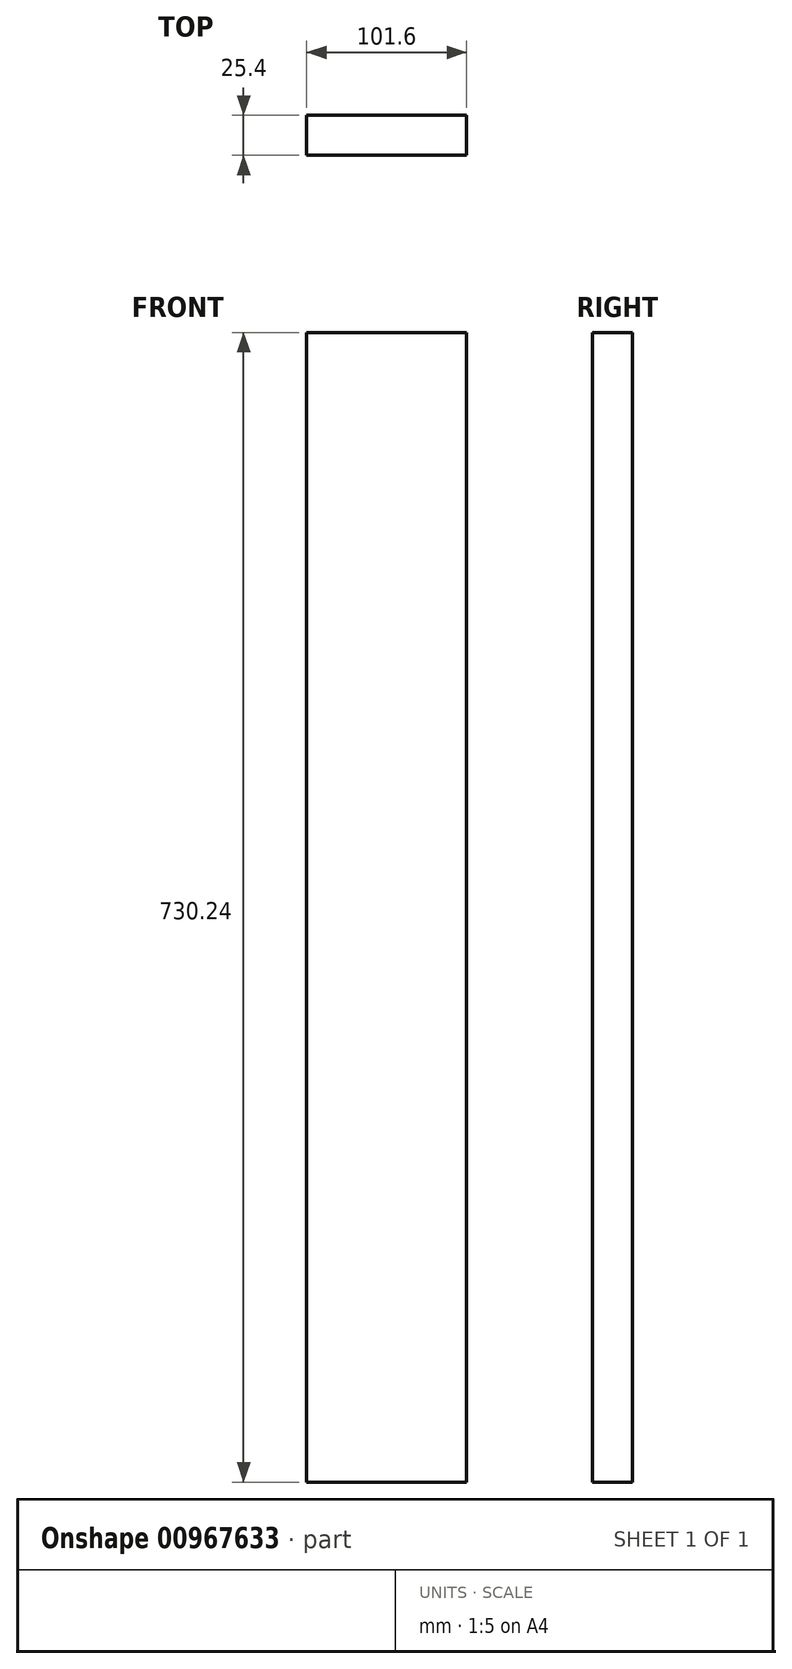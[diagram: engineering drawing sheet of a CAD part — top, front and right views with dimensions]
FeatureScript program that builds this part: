
annotation { "Feature Type Name" : "Feature", "Feature Type Description" : "" }
export const myFeature = defineFeature(function(context is Context, id is Id, definition is map)
    precondition{}
    {
        {
            var Q0;
            Q0=qCreatedBy(makeId("Front.planeOp"),FACE);
            var sketch = newSketch(context, id + "F0", { "sketchPlane" : qUnion([Q0])});
            skLineSegment(sketch, "E0.bottom", {"start": v(50.8, 365.12) * mm, "end": v(-50.8, 365.12) * mm});
            skLineSegment(sketch, "E0.top", {"start": v(50.8, -365.13) * mm, "end": v(-50.8, -365.13) * mm});
            skLineSegment(sketch, "E0.left", {"start": v(50.8, 365.12) * mm, "end": v(50.8, -365.13) * mm});
            skLineSegment(sketch, "E0.right", {"start": v(-50.8, 365.12) * mm, "end": v(-50.8, -365.13) * mm});
            skPoint(sketch, "E0.middle", {"position": v(0, 0) * mm});
            skSolve(sketch);
        }
        {
            var Q0;
            Q0 = qSketchRegion(id + "F0", true);
            extrude(context, id + "F1", {"entities" : qUnion([Q0]), "depth" : 25.4 * mm, "offsetDistance" : 25.4 * mm});
        }
    });
